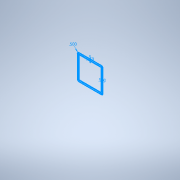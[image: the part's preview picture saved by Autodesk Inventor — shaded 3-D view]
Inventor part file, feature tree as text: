
AUTODESK INVENTOR PART (.ipt)
format: ipt  version: 2021 (Build 250183000, 183)  size: 423,936 bytes
history: native  units: in
note: dims shown in document units (in); Inventor stores cm internally (conversion verified against a paired STEP export)
features: other x3, plane x2, sketch x2, extrude x1, loft x1
ambient origin geometry x8: Origin, YZ Plane, XZ Plane, XY Plane, X Axis, Y Axis, Z Axis, Center Point
bodies: Body1 (feature_tree)
feature tree (9):
  plane  "Work Plane1"
  sketch  "Sketch1"  dims[d0=1.0in d1=0.5in]
  plane  "Work Plane2"
  sketch  "Sketch2"  dims[d2=0.0625in d5=1.0in d6=0.0in d7=0.0in d8=90.0deg d9=0.0in d10=90.0deg]
  extrude  "Extrusion2"  Depth=0.5in
  loft  "Loft1"
  other  "<userpath>\Documents\FSAE\Lafayette-Motorsports\FullCarV2.0.iam"
  other  "FullCarV2.0.iam"
  other  "MidBody:1"
